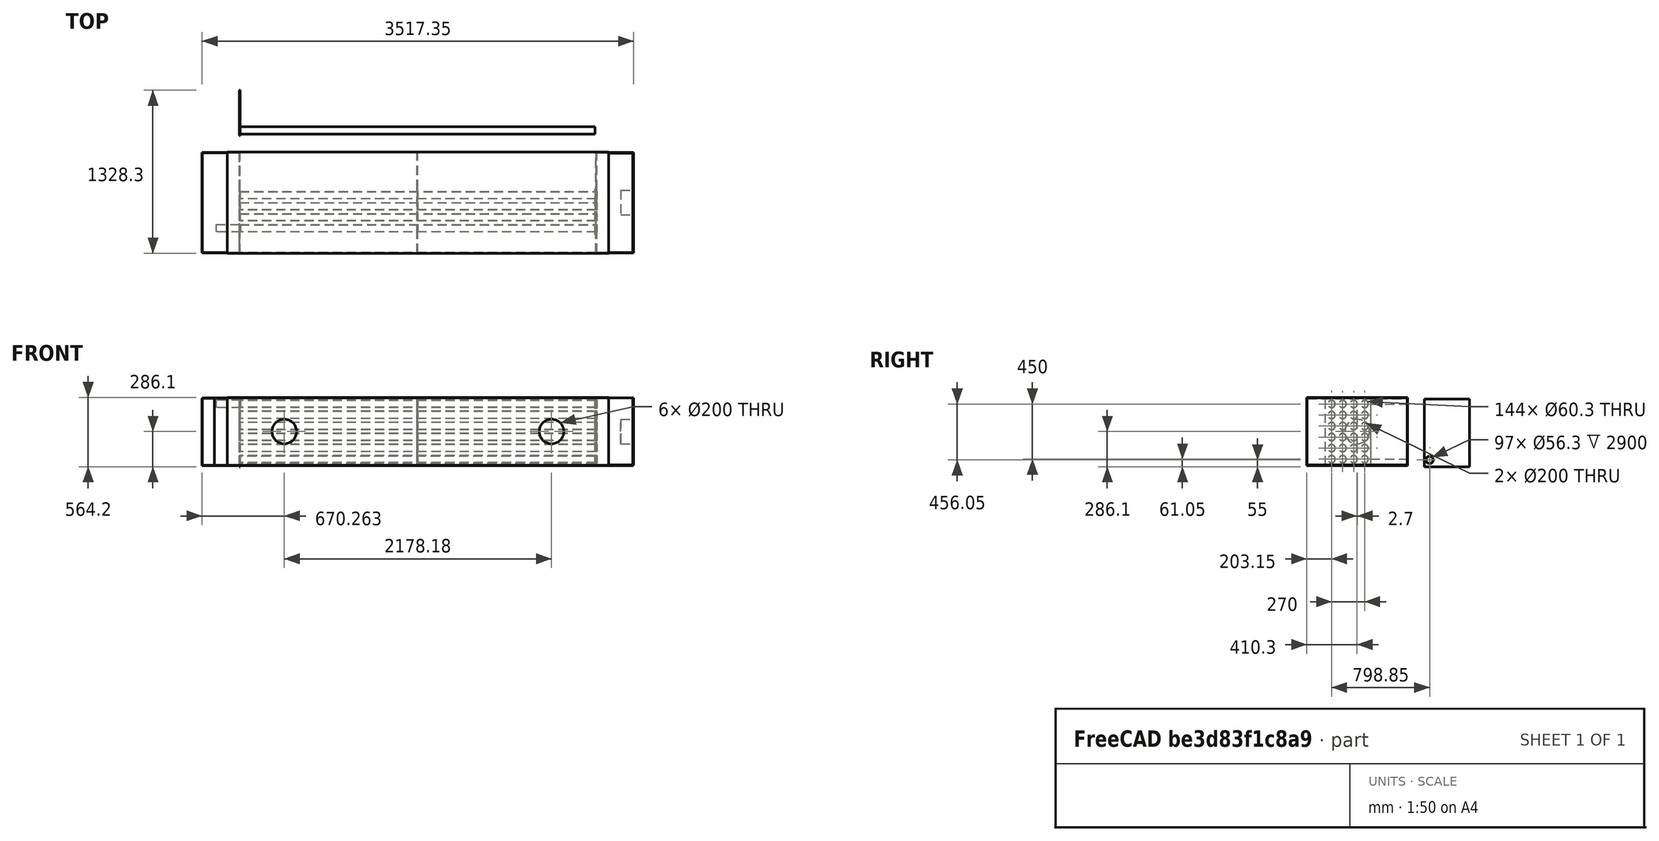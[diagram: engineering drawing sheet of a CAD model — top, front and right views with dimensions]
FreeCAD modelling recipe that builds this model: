
FCSTD DOCUMENT  (FreeCAD 0.18.4R)
Label: intercambiador
License: All rights reserved
LicenseURL: http://en.wikipedia.org/wiki/All_rights_reserved
objects: Part::Box×23, TechDraw::DrawViewDimension×21, Part::Feature×20, Part::Cut×11, TechDraw::DrawViewPart×10, Part::MultiFuse×8, Sketcher::SketchObject×6, Part::Part2DObjectPython×5, TechDraw::DrawHatch×5, PartDesign::Pad×4, PartDesign::Body×4, Part::FeaturePython×4, TechDraw::DrawSVGTemplate×4, TechDraw::DrawPage×4, Part::Fuse×3, App::DocumentObjectGroup×2
note: 92 computed .brp shape members not serialized (recipe doc carries the construction recipe); baked Part::Feature solids carry a one-line shape summary decoded from their .brp

FEATURE [Sketcher::SketchObject] Sketch
  MapMode = 5
  Placement = pos=(0,0,0) rot=(0.57735,0.57735,0.57735;2.0944rad)
  Support = -> [YZ_Plane]
  sketch-geometry (2):
    g0: Circle CenterX=0 CenterY=0 CenterZ=0 NormalX=0 NormalY=0 NormalZ=1 AngleXU=0 Radius=30.15
    g1: Circle CenterX=0 CenterY=0 CenterZ=0 NormalX=0 NormalY=0 NormalZ=1 AngleXU=0 Radius=28.15
  constraints (2):
    c: Diameter(g0) = 60.3
    c: Diameter(g1) = 56.3
FEATURE [PartDesign::Pad] Pad
  Length = 2900
  Length2 = 100
  Placement = pos=(0,0,0) rot=(0.57735,0.57735,0.57735;2.0944rad)
  Profile = -> Sketch
  Type = 0
FEATURE [Sketcher::SketchObject] Sketch001
  MapMode = 5
  Placement = pos=(0,0,0) rot=(0.57735,0.57735,0.57735;2.0944rad)
  Support = -> [YZ_Plane]
  sketch-geometry (1):
    g0: Circle CenterX=0 CenterY=0 CenterZ=0 NormalX=0 NormalY=0 NormalZ=1 AngleXU=0 Radius=30.15
  constraints (1):
    c: Diameter(g0) = 60.3
FEATURE [PartDesign::Body] Body  label="Tubo"
  Group = -> [Sketch,Pad,Sketch001]
  Origin = -> Origin
  Tip = -> Pad
FEATURE [Sketcher::SketchObject] Sketch002
  MapMode = 5
  Placement = pos=(0,0,0) rot=(0.57735,0.57735,0.57735;2.0944rad)
  Support = -> [YZ_Plane001]
  sketch-geometry (1):
    g0: Circle CenterX=0 CenterY=0 CenterZ=0 NormalX=0 NormalY=0 NormalZ=1 AngleXU=0 Radius=30.15
  constraints (1):
    c: Diameter(g0) = 60.3
FEATURE [PartDesign::Pad] Pad001
  Length = 200
  Length2 = 100
  Placement = pos=(0,0,0) rot=(0.57735,0.57735,0.57735;2.0944rad)
  Profile = -> Sketch002
  Type = 0
FEATURE [PartDesign::Body] Body001  label="macho_tubo"
  Group = -> [Sketch002,Pad001]
  Origin = -> Origin001
  Placement = pos=(-418,209,0) rot=(0,0,1;0rad)
  Tip = -> Pad001
FEATURE [Part::FeaturePython] Array  label="paquete_tubos"  # Draft array (typed FeaturePython)
  Angle = 360
  ArrayType = 0
  Axis = (0,0,1)
  Base = -> Pad
  Center = (0,0,0)
  Fuse = false
  IntervalAxis = (0,0,0)
  IntervalX = (0,0,0)
  IntervalY = (0,90,0)
  IntervalZ = (0,0,90)
  NumberPolar = 0
  NumberX = 4
  NumberY = 4
  NumberZ = 6
  Placement = pos=(6.35,-798.85,6.05) rot=(0,0,1;0rad)
FEATURE [Part::FeaturePython] Array001  label="paquete_macho"  # Draft array (typed FeaturePython)
  Angle = 360
  ArrayType = 0
  Axis = (0,0,1)
  Base = -> Body001
  Center = (0,0,0)
  Fuse = false
  IntervalAxis = (0,0,0)
  IntervalX = (1,0,0)
  IntervalY = (0,90,0)
  IntervalZ = (0,0,90)
  NumberPolar = 1
  NumberX = 2
  NumberY = 4
  NumberZ = 6
  Placement = pos=(228.35,-1007.85,6.05) rot=(0,0,1;0rad)
FEATURE [Part::Box] Box  label="Cubo"
  AttacherType = Attacher::AttachEngine3D
  Height = 550.2
  Length = 6.35
  Placement = pos=(0,-44,-55) rot=(0,0,1;0rad)
  Width = 370.3
FEATURE [Part::Box] Box001  label="Cubo001"
  AttacherType = Attacher::AttachEngine3D
  Height = 550.2
  Length = 6.35
  Placement = pos=(0,-849,-44) rot=(0,0,1;0rad)
  Width = 370.3
FEATURE [Part::Feature] Pad004
  Placement = pos=(-188.65,-798.85,456.05) rot=(0.57735,0.57735,0.57735;2.0944rad)
  shape: bbox 200 x 60.3 x 60.3 mm, 3 faces (baked)
FEATURE [Sketcher::SketchObject] Sketch003
  MapMode = 5
  Placement = pos=(6.35,-849,-44) rot=(0.57735,0.57735,0.57735;2.0944rad)
  Support = -> [Box001]
FEATURE [Part::Cut] Cut  label="Placa portatubo"
  Base = -> Box001
  Tool = -> Array001
FEATURE [Sketcher::SketchObject] Sketch004
  MapMode = 5
  Placement = pos=(0,0,0) rot=(0.57735,0.57735,0.57735;2.0944rad)
  Support = -> [YZ_Plane003]
  sketch-geometry (1):
    g0: Circle CenterX=0 CenterY=0 CenterZ=0 NormalX=0 NormalY=0 NormalZ=1 AngleXU=0 Radius=30.15
  constraints (1):
    c: Diameter(g0) = 60.3
FEATURE [PartDesign::Pad] Pad005
  Length = 200
  Length2 = 100
  Placement = pos=(0,0,0) rot=(0.57735,0.57735,0.57735;2.0944rad)
  Profile = -> Sketch004
  Type = 0
FEATURE [PartDesign::Body] Body002  label="macho_tubo001"
  Group = -> [Sketch004,Pad005]
  Origin = -> Origin002
  Placement = pos=(-418,209,0) rot=(0,0,1;0rad)
  Tip = -> Pad005
FEATURE [Part::Box] Box002  label="Cubo002"
  AttacherType = Attacher::AttachEngine3D
  Height = 550.2
  Length = 6.35
  Placement = pos=(0,-849,-44) rot=(0,0,1;0rad)
  Width = 370.3
FEATURE [Part::FeaturePython] Array002  label="paquete_macho001"  # Draft array (typed FeaturePython)
  Angle = 360
  ArrayType = 0
  Axis = (0,0,1)
  Base = -> Body002
  Center = (0,0,0)
  Fuse = false
  IntervalAxis = (0,0,0)
  IntervalX = (1,0,0)
  IntervalY = (0,90,0)
  IntervalZ = (0,0,90)
  NumberPolar = 1
  NumberX = 2
  NumberY = 4
  NumberZ = 6
  Placement = pos=(228.35,-1007.85,6.05) rot=(0,0,1;0rad)
FEATURE [Part::Cut] Cut001  label="Placa portatubo001"
  Base = -> Box002
  Placement = pos=(1450,1.14e-13,0) rot=(0,0,1;0rad)
  Tool = -> Array002
FEATURE [Sketcher::SketchObject] Sketch005
  MapMode = 5
  Placement = pos=(0,0,0) rot=(0.57735,0.57735,0.57735;2.0944rad)
  Support = -> [YZ_Plane004]
  sketch-geometry (1):
    g0: Circle CenterX=0 CenterY=0 CenterZ=0 NormalX=0 NormalY=0 NormalZ=1 AngleXU=0 Radius=30.15
  constraints (1):
    c: Diameter(g0) = 60.3
FEATURE [PartDesign::Pad] Pad006
  Length = 200
  Length2 = 100
  Placement = pos=(0,0,0) rot=(0.57735,0.57735,0.57735;2.0944rad)
  Profile = -> Sketch005
  Type = 0
FEATURE [PartDesign::Body] Body003  label="macho_tubo002"
  Group = -> [Sketch005,Pad006]
  Origin = -> Origin003
  Placement = pos=(-418,209,0) rot=(0,0,1;0rad)
  Tip = -> Pad006
FEATURE [Part::Box] Box003  label="Cubo003"
  AttacherType = Attacher::AttachEngine3D
  Height = 550.2
  Length = 6.35
  Placement = pos=(0,-849,-44) rot=(0,0,1;0rad)
  Width = 370.3
FEATURE [Part::FeaturePython] Array003  label="paquete_macho002"  # Draft array (typed FeaturePython)
  Angle = 360
  ArrayType = 0
  Axis = (0,0,1)
  Base = -> Body003
  Center = (0,0,0)
  Fuse = false
  IntervalAxis = (0,0,0)
  IntervalX = (1,0,0)
  IntervalY = (0,90,0)
  IntervalZ = (0,0,90)
  NumberPolar = 1
  NumberX = 2
  NumberY = 4
  NumberZ = 6
  Placement = pos=(228.35,-1007.85,6.05) rot=(0,0,1;0rad)
FEATURE [Part::Cut] Cut002  label="Placa portatubo002"
  Base = -> Box003
  Placement = pos=(2900,1.78e-13,0) rot=(0,0,1;0rad)
  Tool = -> Array003
FEATURE [Part::Box] Box004  label="Cubo004"
  AttacherType = Attacher::AttachEngine3D
  Height = 550.2
  Length = 6.35
  Placement = pos=(0,-478.7,-44) rot=(0,0,1;0rad)
  Width = 297
FEATURE [Part::MultiFuse] Fusion
  Shapes = -> [Cut,Box004]
FEATURE [Part::Box] Box005  label="entrada_porta_tubos"
  AttacherType = Attacher::AttachEngine3D
  Height = 550.2
  Length = 6.35
  Placement = pos=(0,-999,-44) rot=(0,0,1;0rad)
  Width = 150
FEATURE [Part::Fuse] Fusion001  label="placa_portatubo1"
  Base = -> Fusion
  Tool = -> Box005
FEATURE [Part::Box] Box006  label="entrada_porta_tubos001"
  AttacherType = Attacher::AttachEngine3D
  Height = 550.2
  Length = 6.35
  Placement = pos=(1450,-999,-44) rot=(0,0,1;0rad)
  Width = 150
FEATURE [Part::Box] Box007  label="chapa_carcasa_1"
  AttacherType = Attacher::AttachEngine3D
  Height = 550.2
  Length = 3
  Placement = pos=(2906.35,-999,-44) rot=(0,0,1;1.5708rad)
  Width = 2900
FEATURE [Part::Box] Box008  label="carcasa_fondo"
  AttacherType = Attacher::AttachEngine3D
  Height = 550.2
  Length = 3
  Placement = pos=(3011.35,-1002,-44) rot=(0,0,1;1.5708rad)
  Width = 3110
FEATURE [Part::Box] Box009  label="refuerzo_1"
  AttacherType = Attacher::AttachEngine3D
  Height = 50
  Length = 6.35
  Placement = pos=(1450,-478.7,-44) rot=(0,0,1;0rad)
  Width = 297
FEATURE [Part::Feature] Cylinder001  label="agujero_entrada"
  Placement = pos=(367.262,-899,231.1) rot=(1,0,0;1.5708rad)
  shape: bbox 200 x 100 x 200 mm, 3 faces (baked)
FEATURE [Part::Part2DObjectPython] Line  # Draft 2D object (typed FeaturePython)
  ChamferSize = 0
  Closed = false
  End = (1450,-478.7,506.2)
  FilletRadius = 0
  Length = 1443.65
  MakeFace = false
  Placement = pos=(6.35,-478.7,506.2) rot=(0,0,1;0rad)
  Points = (2) [(0,0,0),(1443.65,5.68434e-14,0)]
  Start = (6.35,-478.7,506.2)
  Subdivisions = 0
  Support = -> [Box007]
FEATURE [Part::Part2DObjectPython] Line002  # Draft 2D object (typed FeaturePython)
  ChamferSize = 0
  Closed = false
  End = (728.175,-999,506.2)
  FilletRadius = 0
  Length = 721.825
  MakeFace = false
  Placement = pos=(6.35,-999,506.2) rot=(0,0,1;0rad)
  Points = (2) [(0,0,0),(721.825,-1.13687e-13,0)]
  Start = (6.35,-999,506.2)
  Subdivisions = 0
FEATURE [Part::Part2DObjectPython] Line004  # Draft 2D object (typed FeaturePython)
  ChamferSize = 0
  Closed = false
  End = (367.262,-999,-44)
  FilletRadius = 0
  Length = 550.2
  MakeFace = false
  Placement = pos=(367.262,-999,506.2) rot=(0,0,1;0rad)
  Points = (2) [(0,0,0),(0,0,-550.2)]
  Start = (367.262,-999,506.2)
  Subdivisions = 0
  Support = -> [Cylinder001]
FEATURE [Part::Part2DObjectPython] Line005  # Draft 2D object (typed FeaturePython)
  ChamferSize = 0
  Closed = false
  End = (2545.44,-181.7,-44)
  FilletRadius = 0
  Length = 550.2
  MakeFace = false
  Placement = pos=(2545.44,-181.7,506.2) rot=(0,0,1;0rad)
  Points = (2) [(0,0,0),(0,0,-550.2)]
  Start = (2545.44,-181.7,506.2)
  Subdivisions = 0
  Support = -> [Cylinder001]
FEATURE [Part::Feature] Cylinder002  label="agujero_entrada2"
  Placement = pos=(2545.44,-911.7,231.1) rot=(1,0,0;1.5708rad)
  shape: bbox 200 x 100 x 200 mm, 3 faces (baked)
FEATURE [Part::Feature] Box013  label="chapa_cabezal2"
  Placement = pos=(3206.35,-999,-44) rot=(0,0,1;1.5708rad)
  shape: bbox 300 x 3 x 550.2 mm, 6 faces (baked)
FEATURE [Part::Box] Box014  label="chapa_cabezal3"
  AttacherType = Attacher::AttachEngine3D
  Height = 544.2
  Length = 3
  Placement = pos=(3206.35,-998.7,-44) rot=(0,0,1;0rad)
  Width = 816
FEATURE [Part::Box] Box015  label="carcasa_lateral1"
  AttacherType = Attacher::AttachEngine3D
  Height = 3
  Length = 3110
  Placement = pos=(-98.65,-1002,506.2) rot=(0,0,1;0rad)
  Width = 823.3
FEATURE [Part::Box] Box016  label="carcasa_lateral2"
  AttacherType = Attacher::AttachEngine3D
  Height = 3
  Length = 3110
  Placement = pos=(-98.65,-1002,-47) rot=(0,0,1;0rad)
  Width = 823.3
FEATURE [Part::Feature] Box017  label="chapa_cabezal003"
  Placement = pos=(3206.35,-999,-44) rot=(0,0,1;1.5708rad)
  shape: bbox 300 x 3 x 550.2 mm, 6 faces (baked)
FEATURE [Part::Feature] Box018  label="chapa_cabezal004"
  Placement = pos=(3206.35,-999,-44) rot=(0,0,1;1.5708rad)
  shape: bbox 300 x 3 x 550.2 mm, 6 faces (baked)
FEATURE [Part::MultiFuse] Fusion003  label="cabezal1"
  Shapes = -> [Box013,Box014]
FEATURE [Part::Box] Box020  label="chapa_cabezal006"
  AttacherType = Attacher::AttachEngine3D
  Height = 547.2
  Length = 3
  Placement = pos=(3211.35,-999,-41) rot=(0,0,1;0rad)
  Width = 817.3
FEATURE [Part::Box] Box021  label="chapa_cabezal007"
  AttacherType = Attacher::AttachEngine3D
  Height = 547.2
  Length = 3
  Placement = pos=(3211.35,-184.7,-41) rot=(0,0,1;1.5708rad)
  Width = 300
FEATURE [Part::Feature] Cylinder003  label="agujero_entrada3"
  Placement = pos=(3109.35,-589,231.1) rot=(0.57735,0.57735,0.57735;2.0944rad)
  shape: bbox 100 x 200 x 200 mm, 3 faces (baked)
FEATURE [Part::Cut] Cut003  label="carcasa_cabezal1"
  Base = -> Fusion003
  Tool = -> Cylinder003
FEATURE [Part::Cut] Cut005
  Base = -> Box007
  Tool = -> Cylinder001
FEATURE [Part::Cut] Cut006  label="carcasa_frente"
  Base = -> Cut005
  Tool = -> Cylinder002
FEATURE [Part::MultiFuse] Fusion005  label="placa_portatubo_centro"
  Shapes = -> [Box006,Cut001]
FEATURE [Part::Fuse] Fusion006
  Base = -> Box009
FEATURE [Part::MultiFuse] Fusion007  label="placa_portatubo_central"
  Shapes = -> [Fusion006,Fusion005]
FEATURE [TechDraw::DrawSVGTemplate] Template
  EditableTexts = AUTHOR_NAME=PDE 2021; DN=DN; DRAWING_TITLE=Paquete de Tubos; FC-DATE=DD/MM/YYYY; FC-REV=REV A; FC-SC=7/100; FC-SH=X / Y; FC-SI=A4; PN=PN
  Height = 210
  Orientation = 1
  Width = 297
FEATURE [TechDraw::DrawViewPart] View  label="Paquete de Tubos"
  CoarseView = false
  Direction = (0,0,1)
  Focus = 100
  HardHidden = false
  IsoCount = 0
  IsoHidden = false
  IsoVisible = false
  LockPosition = false
  Perspective = false
  Rotation = 0
  Scale = 0.06
  ScaleType = 0
  SeamHidden = false
  SeamVisible = false
  SmoothHidden = false
  SmoothVisible = false
  Source = -> [Array]
  X = 114.251
  Y = 104.724
FEATURE [TechDraw::DrawViewDimension] Dimension
  Arbitrary = false
  FormatSpec = %.2f
  LockPosition = false
  MeasureType = 1
  OverTolerance = 0
  References2D = -> [View]
  Rotation = 0
  ScaleType = 0
  Type = 2
  UnderTolerance = 0
  X = -100.92
  Y = 1.32576
FEATURE [TechDraw::DrawViewDimension] Dimension001
  Arbitrary = false
  FormatSpec = %.2f
  LockPosition = false
  MeasureType = 1
  OverTolerance = 0
  References2D = -> [View]
  Rotation = 0
  ScaleType = 0
  Type = 1
  UnderTolerance = 0
  X = 0.363074
  Y = 26.2473
FEATURE [TechDraw::DrawViewPart] View001  label="Paquete Tubos Frontal"
  CoarseView = false
  Direction = (1,0,0)
  Focus = 100
  HardHidden = false
  IsoCount = 0
  IsoHidden = false
  IsoVisible = false
  LockPosition = false
  Perspective = false
  Rotation = 90
  Scale = 0.07
  ScaleType = 0
  SeamHidden = false
  SeamVisible = false
  SmoothHidden = false
  SmoothVisible = false
  Source = -> [Array]
  X = 244.139
  Y = 106.621
FEATURE [TechDraw::DrawViewDimension] Dimension002
  Arbitrary = false
  FormatSpec = %.2f
  LockPosition = false
  MeasureType = 1
  OverTolerance = 0
  References2D = -> [View001]
  Rotation = 0
  ScaleType = 0
  Type = 1
  UnderTolerance = 0
  X = -12.2146
  Y = 30.031
FEATURE [TechDraw::DrawViewDimension] Dimension003
  Arbitrary = false
  FormatSpec = ⌀%.2f
  LockPosition = false
  MeasureType = 1
  OverTolerance = 0
  References2D = -> [View001]
  Rotation = 0
  ScaleType = 0
  Type = 5
  UnderTolerance = 0
  X = 20.9139
  Y = 25.7776
FEATURE [TechDraw::DrawViewDimension] Dimension004
  Arbitrary = false
  FormatSpec = ⌀%.2f
  LockPosition = false
  MeasureType = 1
  OverTolerance = 0
  References2D = -> [View001]
  Rotation = 0
  ScaleType = 0
  Type = 5
  UnderTolerance = 0
  X = 31.2088
  Y = 19.1508
FEATURE [TechDraw::DrawPage] Page  label="Hoja 1 - Tubos"
  KeepUpdated = true
  ProjectionType = 0
  Template = -> Template
  Views = -> [View,Dimension,Dimension001,View001,Dimension002,Dimension003,Dimension004]
FEATURE [TechDraw::DrawSVGTemplate] Template001
  EditableTexts = Designed_by_Name=Designed by Name; Drawing_number=Drawing number; FC-Date=Date; FC-SC=1/10; FC-SH=Sheet; FC-Title=Cabezal y Porta Tubos; Subtitle=Subtitle; Weight=Weight
  Height = 210
  Orientation = 1
  Width = 297
FEATURE [TechDraw::DrawViewPart] View002  label="Cabezal"
  CoarseView = false
  Direction = (1,0,0)
  Focus = 100
  HardHidden = false
  IsoCount = 0
  IsoHidden = false
  IsoVisible = false
  LockPosition = false
  Perspective = false
  Rotation = 0
  Scale = 0.1
  ScaleType = 0
  SeamHidden = false
  SeamVisible = false
  SmoothHidden = false
  SmoothVisible = false
  Source = -> [Cut003]
  X = 229.134
  Y = 163.927
FEATURE [TechDraw::DrawViewDimension] Dimension005
  Arbitrary = false
  FormatSpec = %.2f
  LockPosition = false
  MeasureType = 1
  OverTolerance = 0
  References2D = -> [View002]
  Rotation = 0
  ScaleType = 0
  Type = 2
  UnderTolerance = 0
  X = -48.6582
  Y = -0.38361
FEATURE [TechDraw::DrawViewDimension] Dimension006
  Arbitrary = false
  FormatSpec = %.2f
  LockPosition = false
  MeasureType = 1
  OverTolerance = 0
  References2D = -> [View002]
  Rotation = 0
  ScaleType = 0
  Type = 1
  UnderTolerance = 0
  X = -1.90393
  Y = 33.0346
FEATURE [TechDraw::DrawViewPart] View004  label="Placa Porta Tubos Central"
  CoarseView = false
  Direction = (1,0,0)
  Focus = 100
  HardHidden = false
  IsoCount = 0
  IsoHidden = false
  IsoVisible = false
  LockPosition = false
  Perspective = false
  Rotation = 0
  Scale = 0.1
  ScaleType = 0
  SeamHidden = false
  SeamVisible = false
  SmoothHidden = false
  SmoothVisible = false
  Source = -> [Fusion007]
  X = 70.6764
  Y = 84.122
FEATURE [TechDraw::DrawViewDimension] Dimension010
  Arbitrary = false
  FormatSpec = %.2f
  LockPosition = false
  MeasureType = 1
  OverTolerance = 0
  References2D = -> [View004]
  Rotation = 0
  ScaleType = 0
  Type = 1
  UnderTolerance = 0
  X = 27.8304
  Y = -40.5807
FEATURE [TechDraw::DrawViewDimension] Dimension011
  Arbitrary = false
  FormatSpec = %.2f
  LockPosition = false
  MeasureType = 1
  OverTolerance = 0
  References2D = -> [View004]
  Rotation = 0
  ScaleType = 0
  Type = 1
  UnderTolerance = 0
  X = -18.2677
  Y = -40.2176
FEATURE [TechDraw::DrawViewDimension] Dimension012
  Arbitrary = false
  FormatSpec = %.2f
  LockPosition = false
  MeasureType = 1
  OverTolerance = 0
  References2D = -> [View004]
  Rotation = 0
  ScaleType = 0
  Type = 2
  UnderTolerance = 0
  X = -49.0026
  Y = 0.726147
FEATURE [TechDraw::DrawHatch] Hatch  label="HatchF1"
  DirProjection = (0,0,1)
  HatchPattern = <path>
  Source = -> View002 [Face1]
FEATURE [TechDraw::DrawHatch] Hatch004  label="Hatch004F2"
  DirProjection = (0,0,1)
  HatchPattern = <path>
  Source = -> View004 [Face2,Face1,Face4,Edge0,Face3]
FEATURE [TechDraw::DrawHatch] Hatch005  label="Hatch005F1"
  DirProjection = (0,0,1)
  HatchPattern = <path>
  Source = -> View004 [Face1]
FEATURE [TechDraw::DrawHatch] Hatch006  label="Hatch006F4"
  DirProjection = (0,0,1)
  HatchPattern = <path>
  Source = -> View004 [Face4]
FEATURE [TechDraw::DrawHatch] Hatch007  label="Hatch007F3"
  DirProjection = (0,0,1)
  HatchPattern = <path>
  Source = -> View004 [Face3]
FEATURE [TechDraw::DrawSVGTemplate] Template002
  EditableTexts = AUTHOR_NAME=PDE 2021; DN=DN; DRAWING_TITLE=Laterales; FC-DATE=DD/MM/YYYY; FC-REV=REV A; FC-SC=7/100; FC-SH=X / Y; FC-SI=A4; FreeCAD_DRAWING=chapa espesor 3mm; PN=PN
  Height = 210
  Orientation = 1
  Width = 297
FEATURE [TechDraw::DrawViewPart] View005
  CoarseView = false
  Direction = (0,-1,0)
  Focus = 100
  HardHidden = false
  IsoCount = 0
  IsoHidden = false
  IsoVisible = false
  LockPosition = false
  Perspective = false
  Rotation = 0
  ScaleType = 0
  SeamHidden = false
  SeamVisible = false
  SmoothHidden = false
  SmoothVisible = false
  Source = -> [Cut003]
  X = 148.5
  Y = 105
FEATURE [TechDraw::DrawViewPart] View006  label="Lateral 1"
  CoarseView = false
  Direction = (0,-1,0)
  Focus = 100
  HardHidden = false
  IsoCount = 0
  IsoHidden = false
  IsoVisible = false
  LockPosition = false
  Perspective = false
  Rotation = 0
  Scale = 0.07
  ScaleType = 0
  SeamHidden = false
  SeamVisible = false
  SmoothHidden = false
  SmoothVisible = false
  Source = -> [Cut006,Cut003]
  X = 146.909
  Y = 161.08
FEATURE [TechDraw::DrawViewDimension] Dimension013
  Arbitrary = false
  FormatSpec = ⌀%.2f
  LockPosition = false
  MeasureType = 1
  OverTolerance = 0
  References2D = -> [View006]
  Rotation = 0
  ScaleType = 0
  Type = 5
  UnderTolerance = 0
  X = -49.5514
  Y = 9.98032
FEATURE [TechDraw::DrawViewDimension] Dimension014
  Arbitrary = false
  FormatSpec = %.2f
  LockPosition = false
  MeasureType = 1
  OverTolerance = 0
  References2D = -> [View006]
  Rotation = 0
  ScaleType = 0
  Type = 1
  UnderTolerance = 0
  X = -1.08922
  Y = -33.4169
FEATURE [TechDraw::DrawViewDimension] Dimension015
  Arbitrary = false
  FormatSpec = %.2f
  LockPosition = false
  MeasureType = 1
  OverTolerance = 0
  References2D = -> [View006]
  Rotation = 0
  ScaleType = 0
  Type = 1
  UnderTolerance = 0
  X = -1.59312
  Y = 25.0662
FEATURE [TechDraw::DrawViewPart] View007  label="Lateral 2"
  CoarseView = false
  Direction = (0,1,0)
  Focus = 100
  HardHidden = false
  IsoCount = 0
  IsoHidden = false
  IsoVisible = false
  LockPosition = false
  Perspective = false
  Rotation = 0
  Scale = 0.07
  ScaleType = 0
  SeamHidden = false
  SeamVisible = false
  SmoothHidden = false
  SmoothVisible = false
  Source = -> [Box008,Cut003]
  X = 146.909
  Y = 86.7045
FEATURE [TechDraw::DrawViewDimension] Dimension016
  Arbitrary = false
  FormatSpec = %.2f
  LockPosition = false
  MeasureType = 1
  OverTolerance = 0
  References2D = -> [View007]
  Rotation = 0
  ScaleType = 0
  Type = 1
  UnderTolerance = 0
  X = -0.397727
  Y = 26.0184
FEATURE [TechDraw::DrawViewDimension] Dimension017
  Arbitrary = false
  FormatSpec = %.2f
  LockPosition = false
  MeasureType = 1
  OverTolerance = 0
  References2D = -> [View007]
  Rotation = 0
  ScaleType = 0
  Type = 2
  UnderTolerance = 0
  X = -130.887
  Y = -0.795455
FEATURE [TechDraw::DrawViewDimension] Dimension018
  Arbitrary = false
  FormatSpec = %.2f
  LockPosition = false
  MeasureType = 1
  OverTolerance = 0
  References2D = -> [View006]
  Rotation = 0
  ScaleType = 0
  Type = 2
  UnderTolerance = 0
  X = -130.887
  Y = 0
FEATURE [TechDraw::DrawPage] Page002  label="Laterales"
  KeepUpdated = true
  ProjectionType = 0
  Template = -> Template002
  Views = -> [View005,View006,Dimension013,Dimension014,Dimension015,View007,Dimension016,Dimension017,Dimension018]
FEATURE [Part::Part2DObjectPython] Line006  # Draft 2D object (typed FeaturePython)
  ChamferSize = 0
  Closed = false
  End = (6.35,-999,231.1)
  FilletRadius = 0
  Length = 2900
  MakeFace = false
  Placement = pos=(2906.35,-999,231.1) rot=(0,0,1;0rad)
  Points = (2) [(0,0,0),(-2900,1.13687e-13,0)]
  Start = (2906.35,-999,231.1)
  Subdivisions = 0
  Support = -> [Box016]
FEATURE [Part::Feature] Box023  label="carcasa_fondo001"
  Placement = pos=(2906.35,-999,-44) rot=(0,0,1;1.5708rad)
  shape: bbox 3110 x 3 x 550.2 mm, 6 faces (baked)
FEATURE [Part::Feature] Cylinder006  label="agujero_entrada007"
  Placement = pos=(2545.44,-999,231.1) rot=(0,0.707107,0.707107;3.14159rad)
  shape: bbox 200 x 100 x 200 mm, 3 faces (baked)
FEATURE [Part::Feature] Cylinder007  label="agujero_entrada008"
  Placement = pos=(367.262,-1096,231.1) rot=(0,0.707107,0.707107;3.14159rad)
  shape: bbox 200 x 100 x 200 mm, 3 faces (baked)
FEATURE [Part::Cut] Cut007
  Base = -> Box023
  Tool = -> Cylinder006
FEATURE [Part::Cut] Cut008
  Base = -> Cut007
  Tool = -> Cylinder007
FEATURE [Part::Feature] Cylinder008  label="agujero_entrada009"
  Placement = pos=(2545.44,-1049,231.1) rot=(0,0.707107,0.707107;3.14159rad)
  shape: bbox 200 x 100 x 200 mm, 3 faces (baked)
FEATURE [Part::Feature] Box024  label="carcasa_fondo002"
  Placement = pos=(2906.35,-999,-44) rot=(0,0,1;1.5708rad)
  shape: bbox 3110 x 3 x 550.2 mm, 6 faces (baked)
FEATURE [Part::Box] Box025  label="carcasa_fondo_1"
  AttacherType = Attacher::AttachEngine3D
  Height = 550.2
  Length = 3
  Placement = pos=(3011.35,-181.7,-44) rot=(0,0,1;1.5708rad)
  Width = 3110
FEATURE [Part::MultiFuse] Fusion008  label="Placa portatubos 1 a"
  Shapes = -> [Cut,Box004,Box005]
FEATURE [Part::Feature] Fusion010  label="Placa portatubos 1 a002"
  Placement = pos=(2909.35,2.27e-13,0) rot=(0,0,1;0rad)
  shape: bbox 6.35 x 817.3 x 550.2 mm, 38 faces (baked)
FEATURE [Part::Feature] Box026  label="refuerzo_003"
  Placement = pos=(1450,-478.7,456.2) rot=(0,0,1;0rad)
  shape: bbox 6.35 x 297 x 50 mm, 6 faces (baked)
FEATURE [Part::Fuse] Fusion011
  Base = -> Box009
  Tool = -> Fusion005
FEATURE [Part::MultiFuse] Fusion012  label="placa portatubos central a"
  Shapes = -> [Box026,Fusion011]
FEATURE [Part::Cut] Cut009
  Base = -> Box008
  Tool = -> Cylinder007
FEATURE [Part::Cut] Cut010  label="carcasa_fondo_2"
  Base = -> Cut009
  Tool = -> Cylinder008
FEATURE [Part::Box] Box027  label="chapa_cabezal008"
  AttacherType = Attacher::AttachEngine3D
  Height = 547.2
  Length = 3
  Placement = pos=(3211.35,-999,-41) rot=(0,0,1;1.5708rad)
  Width = 300
FEATURE [TechDraw::DrawViewPart] View008  label="Placa Pora Tubos "
  CoarseView = false
  Direction = (1,0,0)
  Focus = 100
  HardHidden = false
  IsoCount = 0
  IsoHidden = false
  IsoVisible = false
  LockPosition = false
  Perspective = false
  Rotation = 0
  Scale = 0.1
  ScaleType = 0
  SeamHidden = false
  SeamVisible = false
  SmoothHidden = false
  SmoothVisible = false
  Source = -> [Fusion010]
  X = 69.8989
  Y = 164.546
FEATURE [TechDraw::DrawSVGTemplate] Template003
  EditableTexts = AUTHOR_NAME=AUTHOR NAME; DN=DN; DRAWING_TITLE=DRAWING TITLE; FC-DATE=DD/MM/YYYY; FC-REV=REV A; FC-SC=SCALE; FC-SH=X / Y; FC-SI=A4; FreeCAD_DRAWING=FreeCAD DRAWING; PN=PN
  Height = 210
  Orientation = 1
  Width = 297
FEATURE [Part::Feature] Box029  label="chapa_cabezal010"
  Placement = pos=(3206.35,-185.7,-44) rot=(0,0,1;1.5708rad)
  shape: bbox 300 x 3 x 550.2 mm, 6 faces (baked)
FEATURE [Part::Box] Box030  label="chapa_cabezal009"
  AttacherType = Attacher::AttachEngine3D
  Height = 3
  Length = 300
  Placement = pos=(2909.35,-998.7,-47) rot=(0,0,1;0rad)
  Width = 814.3
FEATURE [Part::Box] Box031  label="chapa_cabezal011"
  AttacherType = Attacher::AttachEngine3D
  Height = 3
  Length = 300
  Placement = pos=(2906.35,-996,503.2) rot=(0,0,1;0rad)
  Width = 814.3
FEATURE [App::DocumentObjectGroup] Group  label="Grupo"
  Group = -> [Box029,Box030,Box031,Cut003]
FEATURE [Part::Feature] Box032  label="chapa_cabezal012"
  Placement = pos=(3206.35,-999,-44) rot=(0,0,1;1.5708rad)
  shape: bbox 300 x 3 x 550.2 mm, 6 faces (baked)
FEATURE [Part::Feature] Cylinder009  label="agujero_entrada010"
  Placement = pos=(3109.35,-589,231.1) rot=(0.57735,0.57735,0.57735;2.0944rad)
  shape: bbox 100 x 200 x 200 mm, 3 faces (baked)
FEATURE [Part::Box] Box034  label="chapa_cabezal014"
  AttacherType = Attacher::AttachEngine3D
  Height = 544.2
  Length = 3
  Placement = pos=(3206.35,-998.7,-44) rot=(0,0,1;0rad)
  Width = 816
FEATURE [Part::MultiFuse] Fusion013  label="cabezal002"
  Shapes = -> [Box032,Box034]
FEATURE [Part::Feature] Box035  label="chapa_cabezal015"
  Placement = pos=(3206.35,-999,-44) rot=(0,0,1;1.5708rad)
  shape: bbox 300 x 3 x 550.2 mm, 6 faces (baked)
FEATURE [Part::Feature] Cylinder010  label="agujero_entrada011"
  Placement = pos=(3109.35,-589,231.1) rot=(0.57735,0.57735,0.57735;2.0944rad)
  shape: bbox 100 x 200 x 200 mm, 3 faces (baked)
FEATURE [Part::Feature] Box036  label="chapa_cabezal016"
  Placement = pos=(-300,-995,-44) rot=(0,0,-1;1.5708rad)
  shape: bbox 300 x 3 x 550.2 mm, 6 faces (baked)
FEATURE [Part::Box] Box037  label="chapa_cabezal017"
  AttacherType = Attacher::AttachEngine3D
  Height = 544.2
  Length = 3
  Placement = pos=(3206.35,-998.7,-44) rot=(0,0,1;0rad)
  Width = 816
FEATURE [Part::MultiFuse] Fusion014  label="cabezal003"
  Shapes = -> [Box035,Box037]
FEATURE [Part::Box] Box038  label="chapa_cabezal018"
  AttacherType = Attacher::AttachEngine3D
  Height = 3
  Length = 300
  Placement = pos=(-3,-182,-47) rot=(0,0,1;3.14159rad)
  Width = 814.3
FEATURE [Part::Box] Box039  label="chapa_cabezal019"
  AttacherType = Attacher::AttachEngine3D
  Height = 3
  Length = 300
  Placement = pos=(1.137e-13,-184.7,503.2) rot=(0,0,1;3.14159rad)
  Width = 814.3
FEATURE [Part::Cut] Cut011  label="carcasa_cabezal002"
  Base = -> Fusion014
  Placement = pos=(2906.35,-1180.7,0) rot=(0,0,1;3.14159rad)
  Tool = -> Cylinder010
FEATURE [App::DocumentObjectGroup] Group001  label="Grupo001"
  Group = -> [Box036,Box038,Box039,Cut011]
FEATURE [TechDraw::DrawViewPart] View009
  CoarseView = false
  Direction = (0,0,1)
  Focus = 100
  HardHidden = false
  IsoCount = 0
  IsoHidden = false
  IsoVisible = false
  LockPosition = false
  Perspective = false
  Rotation = 0
  Scale = 0.07
  ScaleType = 0
  SeamHidden = false
  SeamVisible = false
  SmoothHidden = false
  SmoothVisible = false
  Source = -> [Box015,Group,Group001]
  X = 145.324
  Y = 151.049
FEATURE [TechDraw::DrawViewDimension] Dimension019
  Arbitrary = false
  FormatSpec = %.2f
  LockPosition = false
  MeasureType = 1
  OverTolerance = 0
  References2D = -> [View009]
  Rotation = 0
  ScaleType = 0
  Type = 1
  UnderTolerance = 0
  X = -1.19093
  Y = 34.9116
FEATURE [TechDraw::DrawViewDimension] Dimension020
  Arbitrary = false
  FormatSpec = %.2f
  LockPosition = false
  MeasureType = 1
  OverTolerance = 0
  References2D = -> [View009]
  Rotation = 0
  ScaleType = 0
  Type = 2
  UnderTolerance = 0
  X = 129.681
  Y = -1.21543
FEATURE [TechDraw::DrawViewPart] View010
  CoarseView = false
  Direction = (0,-1,0)
  Focus = 100
  HardHidden = false
  IsoCount = 0
  IsoHidden = false
  IsoVisible = false
  LockPosition = false
  Perspective = false
  Rotation = 0
  Scale = 0.07
  ScaleType = 0
  SeamHidden = false
  SeamVisible = false
  SmoothHidden = false
  SmoothVisible = false
  Source = -> [Box013,Cut006,Box036]
  X = 144.927
  Y = 89.121
FEATURE [TechDraw::DrawViewDimension] Dimension021
  Arbitrary = false
  FormatSpec = %.2f
  LockPosition = false
  MeasureType = 1
  OverTolerance = 0
  References2D = -> [View010]
  Rotation = 0
  ScaleType = 0
  Type = 2
  UnderTolerance = 0
  X = 128.28
  Y = -0.793951
FEATURE [TechDraw::DrawViewDimension] Dimension022
  Arbitrary = false
  FormatSpec = %.2f
  LockPosition = false
  MeasureType = 1
  OverTolerance = 0
  References2D = -> [View010]
  Rotation = 0
  ScaleType = 0
  Type = 1
  UnderTolerance = 0
  X = -7.54253
  Y = -10.9205
FEATURE [TechDraw::DrawPage] Page003
  KeepUpdated = true
  ProjectionType = 0
  Template = -> Template003
  Views = -> [View009,Dimension019,Dimension020,View010,Dimension021,Dimension022]
FEATURE [TechDraw::DrawViewDimension] Dimension023
  Arbitrary = false
  FormatSpec = ⌀%.2f
  LockPosition = false
  MeasureType = 1
  OverTolerance = 0
  References2D = -> [View008]
  Rotation = 0
  ScaleType = 0
  Type = 5
  UnderTolerance = 0
  X = 14.0781
  Y = 0.364088
FEATURE [TechDraw::DrawPage] Page001  label="Hoja 2 - Transversales"
  KeepUpdated = true
  ProjectionType = 0
  Template = -> Template001
  Views = -> [View002,Dimension005,Dimension006,View004,Dimension010,Dimension011,Dimension012,View008,Dimension023]
note: 5 file-system paths scrubbed to <path> (originals preserved in the JSON sidecar)
